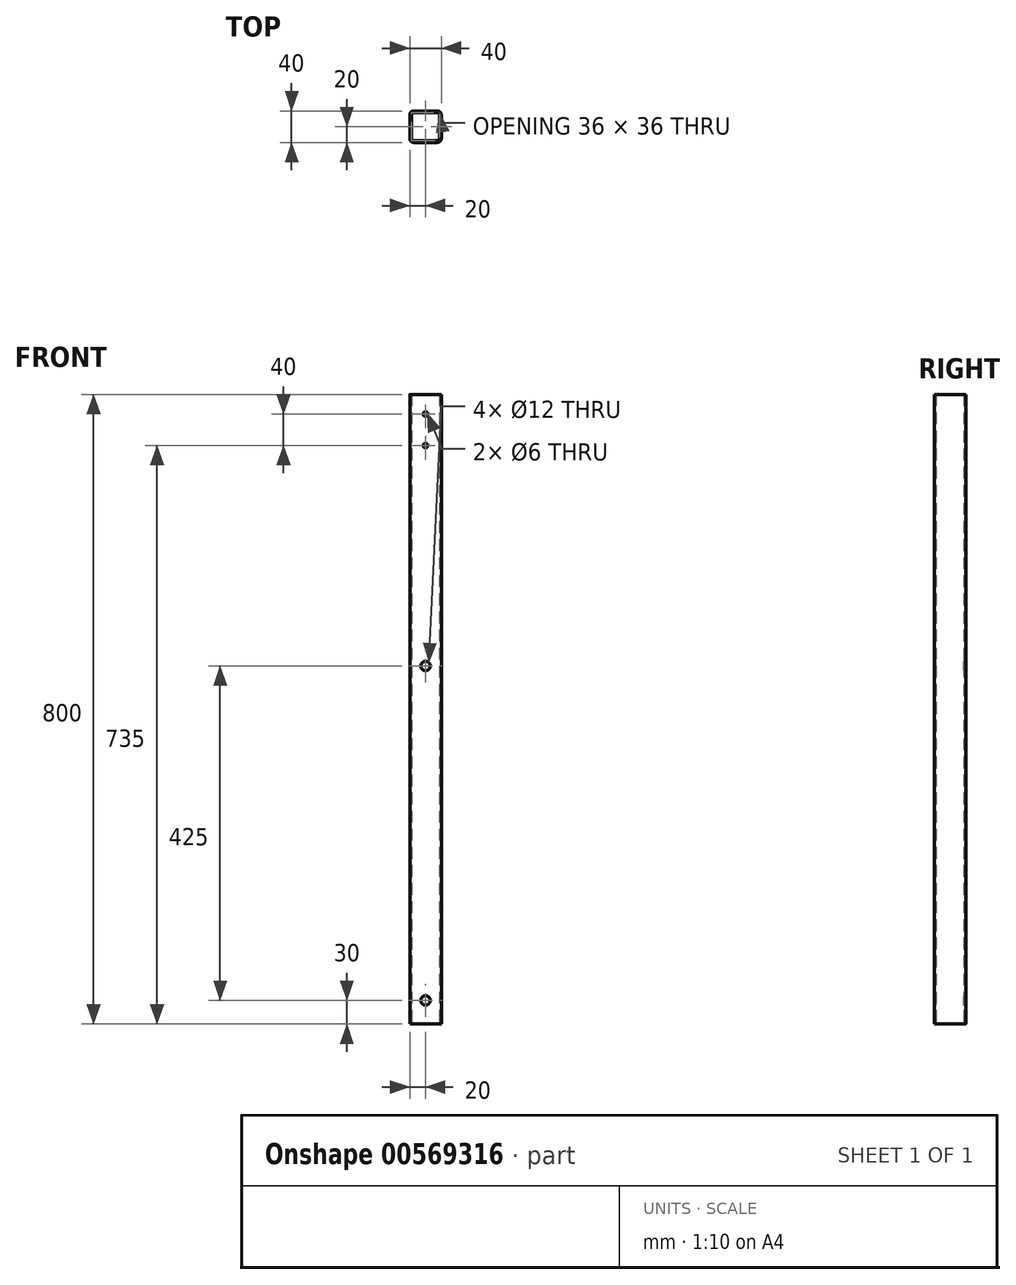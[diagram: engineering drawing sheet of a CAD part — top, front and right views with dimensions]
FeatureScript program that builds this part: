
annotation { "Feature Type Name" : "Feature", "Feature Type Description" : "" }
export const myFeature = defineFeature(function(context is Context, id is Id, definition is map)
    precondition{}
    {
        {
            var Q0;
            Q0=qCreatedBy(makeId("Top.planeOp"),FACE);
            var sketch = newSketch(context, id + "F0", { "sketchPlane" : qUnion([Q0])});
            skLineSegment(sketch, "E0.bottom", {"start": v(15, -20) * mm, "end": v(-15, -20) * mm});
            skLineSegment(sketch, "E0.top", {"start": v(15, 20) * mm, "end": v(-15, 20) * mm});
            skLineSegment(sketch, "E0.left", {"start": v(20, -15) * mm, "end": v(20, 15) * mm});
            skLineSegment(sketch, "E0.right", {"start": v(-20, -15) * mm, "end": v(-20, 15) * mm});
            skPoint(sketch, "E0.middle", {"position": v(0, 0) * mm});
            skPoint(sketch, "E1.visualSharp", {"position": v(-20, 20) * mm});
            skArc(sketch, "E1.filletArc", {"start": v(-15, 20) * mm, "mid": v(-18.54, 18.54) * mm, "end": v(-20, 15) * mm});
            skPoint(sketch, "E2.visualSharp", {"position": v(20, 20) * mm});
            skArc(sketch, "E2.filletArc", {"start": v(20, 15) * mm, "mid": v(18.54, 18.54) * mm, "end": v(15, 20) * mm});
            skPoint(sketch, "E3.visualSharp", {"position": v(20, -20) * mm});
            skArc(sketch, "E3.filletArc", {"start": v(15, -20) * mm, "mid": v(18.54, -18.54) * mm, "end": v(20, -15) * mm});
            skPoint(sketch, "E4.visualSharp", {"position": v(-20, -20) * mm});
            skArc(sketch, "E4.filletArc", {"start": v(-20, -15) * mm, "mid": v(-18.54, -18.54) * mm, "end": v(-15, -20) * mm});
            skLineSegment(sketch, "E5.0", {"start": v(15, -18) * mm, "end": v(-15, -18) * mm});
            skLineSegment(sketch, "E5.1", {"start": v(18, -15) * mm, "end": v(18, 15) * mm});
            skLineSegment(sketch, "E5.2", {"start": v(15, 18) * mm, "end": v(-15, 18) * mm});
            skLineSegment(sketch, "E5.3", {"start": v(-18, -15) * mm, "end": v(-18, 15) * mm});
            skPoint(sketch, "E6.visualSharp", {"position": v(-18, 18) * mm});
            skArc(sketch, "E6.filletArc", {"start": v(-15, 18) * mm, "mid": v(-17.12, 17.12) * mm, "end": v(-18, 15) * mm});
            skPoint(sketch, "E7.visualSharp", {"position": v(18, 18) * mm});
            skArc(sketch, "E7.filletArc", {"start": v(18, 15) * mm, "mid": v(17.12, 17.12) * mm, "end": v(15, 18) * mm});
            skPoint(sketch, "E8.visualSharp", {"position": v(18, -18) * mm});
            skArc(sketch, "E8.filletArc", {"start": v(15, -18) * mm, "mid": v(17.12, -17.12) * mm, "end": v(18, -15) * mm});
            skPoint(sketch, "E9.visualSharp", {"position": v(-18, -18) * mm});
            skArc(sketch, "E9.filletArc", {"start": v(-18, -15) * mm, "mid": v(-17.12, -17.12) * mm, "end": v(-15, -18) * mm});
            skSolve(sketch);
        }
        {
            var Q0;
            Q0 = qSketchRegion(id + "F0", true);
            extrude(context, id + "F1", {"entities" : qUnion([Q0]), "depth" : 800 * mm, "offsetDistance" : 25 * mm});
        }
        {
            var Q0;
            Q0=makeQuery(id+"F1.opExtrude","SWEPT_FACE",FACE,{"disambiguationData":[OSD([sQuery(id+"F0.wireOp",EDGE,"E0.bottom")])]});
            var sketch = newSketch(context, id + "F2", { "sketchPlane" : qUnion([Q0])});
            skLineSegment(sketch, "E10", {"start": v(0, 0) * mm, "end": v(0, 800) * mm, "construction": true});
            skCircle(sketch, "E11", {"center": v(0, 775) * mm, "radius": 3 * mm});
            skCircle(sketch, "E12.0.1.0", {"center": v(0, 735) * mm, "radius": 3 * mm});
            skLineSegment(sketch, "E12.direction1", {"start": v(0, 775) * mm, "end": v(37.72, 779.32) * mm, "construction": true});
            skLineSegment(sketch, "E12.direction2", {"start": v(0, 775) * mm, "end": v(0, 735) * mm, "construction": true});
            skSolve(sketch);
        }
        {
            var Q0;
            Q0 = qSketchRegion(id + "F2", true);
            extrude(context, id + "F3", {"entities" : qUnion([Q0]), "operationType" : NewBodyOperationType.REMOVE, "oppositeDirection" : true, "depth" : 25 * mm, "offsetDistance" : 25 * mm});
        }
        {
            var Q0;
            Q0=qCreatedBy(makeId("Right.planeOp"),FACE);
            var sketch = newSketch(context, id + "F4", { "sketchPlane" : qUnion([Q0])});
            skLineSegment(sketch, "E13", {"start": v(-112.62, 505) * mm, "end": v(-20, 505) * mm});
            skLineSegment(sketch, "E14", {"start": v(-20, -118.36) * mm, "end": v(-20, 505) * mm});
            skSolve(sketch);
        }
        {
            var Q0;
            Q0=makeQuery(id+"F2.imprint","IMPRINT",FACE,{"disambiguationData":[TD([[makeQuery(id+"F2.imprint","IMPRINT",EDGE,{"derivedFrom":sQuery(id+"F2.wireOp",EDGE,"E11")}),-1.0]])]});
            var sketch = newSketch(context, id + "F5", { "sketchPlane" : qUnion([Q0])});
            skCircle(sketch, "E15", {"center": v(0, 455) * mm, "radius": 6 * mm});
            skCircle(sketch, "E16", {"center": v(0, 30) * mm, "radius": 6 * mm});
            skSolve(sketch);
        }
        {
            var Q0;
            Q0 = qSketchRegion(id + "F5", true);
            extrude(context, id + "F6", {"entities" : qUnion([Q0]), "operationType" : NewBodyOperationType.REMOVE, "endBound" : BoundingType.THROUGH_ALL, "oppositeDirection" : true, "depth" : 25 * mm, "offsetDistance" : 25 * mm});
        }
    });
